FREECAD ASSEMBLY — COMPONENT RECIPES ("generated_example_K93-10436_all7_withTarantinorinos")

This assembly document has 7 components, labeled P0..P6 below (a component is one placed body or linked part). 0 of them carry a construction recipe — the FreeCAD feature program that regenerates the part from scratch, quoted from this document or its linked companion documents; the rest are supplied as boundary geometry only. No exploded tour is included for this assembly.
COMPONENT P0 — geometry summary ("Body"; no construction recipe available for this part):
  bounding box: 104.0 x 36.0 x 1.5 mm
  tessellated surface: 8,624 triangles
  volume: 4912 mm^3 (87% of its bounding box)
  symmetry: mirror-symmetric across its y mid-plane
COMPONENT P1 — geometry summary ("Body003"; no construction recipe available for this part):
  bounding box: 36.0 x 20.0 x 8.6 mm
  tessellated surface: 3,082 triangles
  volume: 2231 mm^3 (36% of its bounding box)
COMPONENT P2 — geometry summary ("Body004"; no construction recipe available for this part):
  bounding box: 36.0 x 20.0 x 8.6 mm
  tessellated surface: 3,082 triangles
  volume: 2231 mm^3 (36% of its bounding box)
COMPONENT P3 — geometry summary ("Body005"; no construction recipe available for this part):
  bounding box: 36.0 x 20.0 x 8.6 mm
  tessellated surface: 3,082 triangles
  volume: 2231 mm^3 (36% of its bounding box)
COMPONENT P4 — geometry summary ("Body006"; no construction recipe available for this part):
  bounding box: 36.0 x 20.0 x 8.6 mm
  tessellated surface: 3,082 triangles
  volume: 2231 mm^3 (36% of its bounding box)
COMPONENT P5 — geometry summary ("K93-120"; no construction recipe available for this part):
  bounding box: 121.5 x 104.0 x 36.0 mm
  tessellated surface: 10,148 triangles
  volume: 84663 mm^3 (19% of its bounding box)
  symmetry: 2-fold rotationally symmetric about the y axis; mirror-symmetric across its x mid-plane, z mid-plane
COMPONENT P6 — geometry summary ("Reference_all7 1"; no construction recipe available for this part):
  bounding box: 140.0 x 99.6 x 22.5 mm
  tessellated surface: 175,252 triangles
  volume: 30738 mm^3 (10% of its bounding box)
PROVENANCE & LICENSES
A FreeCAD (.FCStd) document from a public repository crawl; recipes are the document's own serialized feature recipes (and, for linked parts, companion documents' recipes).
License: mit.
